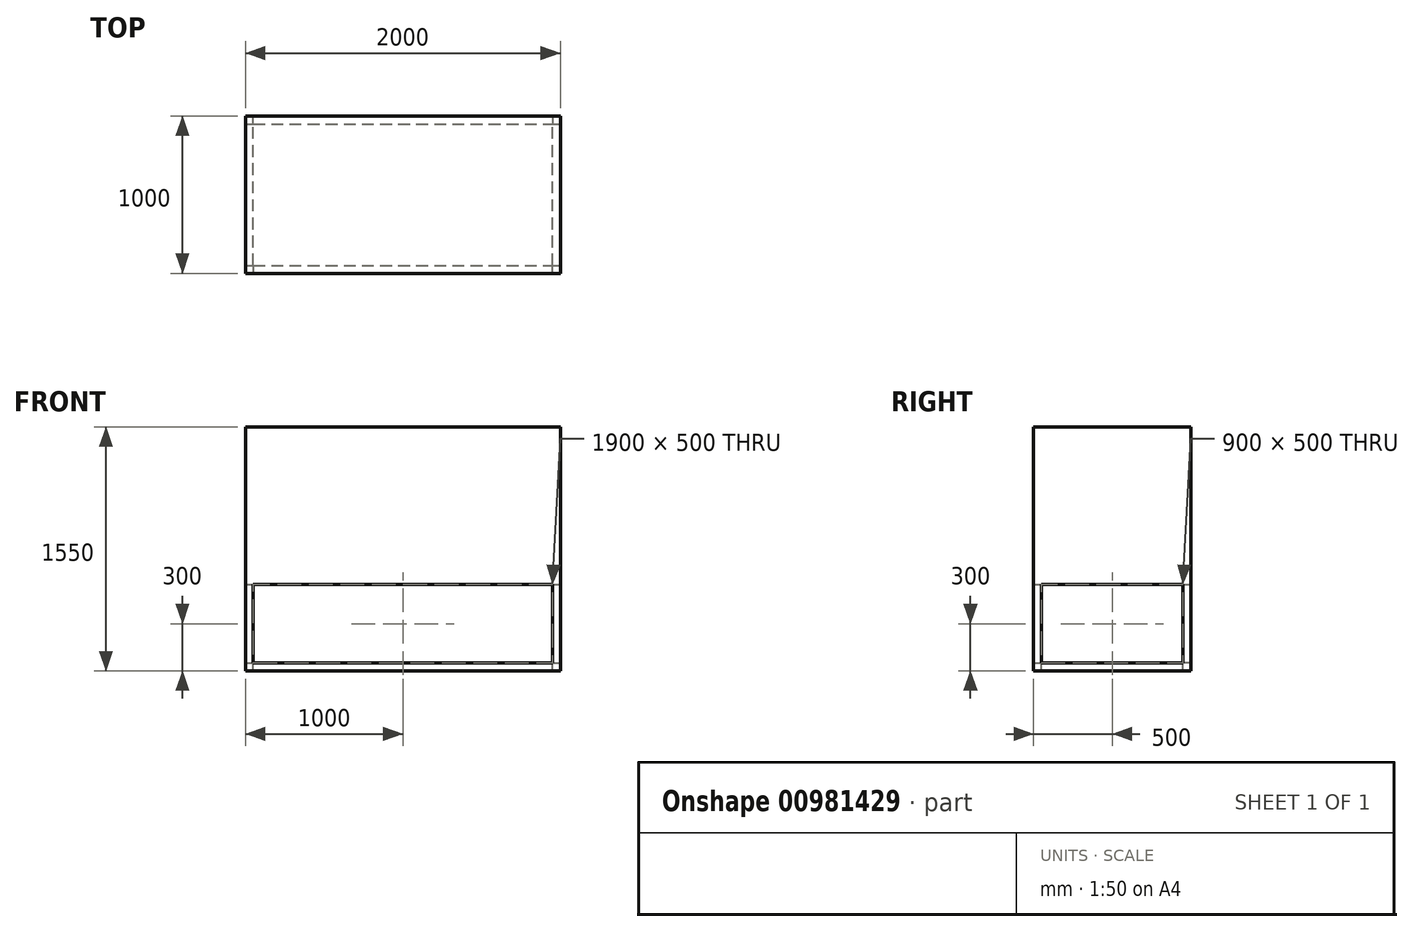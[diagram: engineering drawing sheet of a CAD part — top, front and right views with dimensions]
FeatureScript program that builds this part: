
annotation { "Feature Type Name" : "Feature", "Feature Type Description" : "" }
export const myFeature = defineFeature(function(context is Context, id is Id, definition is map)
    precondition{}
    {
        {
            var Q0;
            Q0=qCreatedBy(makeId("Front.planeOp"),FACE);
            var sketch = newSketch(context, id + "F0", { "sketchPlane" : qUnion([Q0])});
            skLineSegment(sketch, "E0.bottom", {"start": v(-1000, 500) * mm, "end": v(1000, 500) * mm});
            skLineSegment(sketch, "E0.top", {"start": v(-1000, -500) * mm, "end": v(1000, -500) * mm});
            skLineSegment(sketch, "E0.left", {"start": v(-1000, 500) * mm, "end": v(-1000, -500) * mm});
            skLineSegment(sketch, "E0.right", {"start": v(1000, 500) * mm, "end": v(1000, -500) * mm});
            skPoint(sketch, "E0.middle", {"position": v(0, 0) * mm});
            skSolve(sketch);
        }
        {
            var Q0;
            Q0 = qSketchRegion(id + "F0", true);
            extrude(context, id + "F1", {"entities" : qUnion([Q0]), "depth" : 1000 * mm, "offsetDistance" : 25 * mm});
        }
        {
            var Q0;
            Q0=makeQuery(id+"F1.opExtrude","SWEPT_FACE",FACE,{"disambiguationData":[OSD([sQuery(id+"F0.wireOp",EDGE,"E0.top")])]});
            cPlane(context, id + "F2", {"entities" : qUnion([Q0]), "cplaneType" : CPlaneType.OFFSET, "offset" : 0 * mm, "width" : 150 * mm, "height" : 150 * mm});
        }
        {
            var Q0;
            Q0=qCreatedBy(id+"F2.planeOp",FACE);
            var sketch = newSketch(context, id + "F3", { "sketchPlane" : qUnion([Q0])});
            skLineSegment(sketch, "E1", {"start": v(1000, 0) * mm, "end": v(1000, 50) * mm});
            skLineSegment(sketch, "E2", {"start": v(1000, 1000) * mm, "end": v(950, 1000) * mm});
            skLineSegment(sketch, "E3", {"start": v(-1000, 1000) * mm, "end": v(-1000, 950) * mm});
            skLineSegment(sketch, "E4", {"start": v(-1000, 0) * mm, "end": v(-950, 0) * mm});
            skLineSegment(sketch, "E5", {"start": v(-1000, 50) * mm, "end": v(-950, 50) * mm});
            skLineSegment(sketch, "E6", {"start": v(-1000, 950) * mm, "end": v(-950, 950) * mm});
            skLineSegment(sketch, "E7", {"start": v(-950, 950) * mm, "end": v(-950, 1000) * mm});
            skLineSegment(sketch, "E8", {"start": v(950, 1000) * mm, "end": v(950, 950) * mm});
            skLineSegment(sketch, "E9", {"start": v(950, 950) * mm, "end": v(1000, 950) * mm});
            skLineSegment(sketch, "E10", {"start": v(950, 0) * mm, "end": v(950, 50) * mm});
            skLineSegment(sketch, "E11", {"start": v(950, 50) * mm, "end": v(1000, 50) * mm});
            skLineSegment(sketch, "E12", {"start": v(-950, 50) * mm, "end": v(-950, 0) * mm});
            skLineSegment(sketch, "E13.trimOffspring", {"start": v(-950, 1000) * mm, "end": v(-1000, 1000) * mm});
            skLineSegment(sketch, "E14.trimOffspring", {"start": v(1000, 950) * mm, "end": v(1000, 1000) * mm});
            skLineSegment(sketch, "E15.trimOffspring", {"start": v(950, 0) * mm, "end": v(1000, 0) * mm});
            skLineSegment(sketch, "E16.trimOffspring", {"start": v(-1000, 50) * mm, "end": v(-1000, 0) * mm});
            skSolve(sketch);
        }
        {
            var Q0;
            Q0 = qSketchRegion(id + "F3", true);
            extrude(context, id + "F4", {"entities" : qUnion([Q0]), "operationType" : NewBodyOperationType.ADD, "depth" : 500 * mm, "offsetDistance" : 25 * mm});
        }
        {
            var Q0;
            Q0=makeQuery(id+"F4.opExtrude","CAP_FACE",FACE,{"disambiguationData":[OSD([sQuery(id+"F3.wireOp",EDGE,"E3"),sQuery(id+"F3.wireOp",EDGE,"E6"),sQuery(id+"F3.wireOp",EDGE,"E7"),sQuery(id+"F3.wireOp",EDGE,"E13.trimOffspring")])],"isStart":false});
            cPlane(context, id + "F5", {"entities" : qUnion([Q0]), "cplaneType" : CPlaneType.OFFSET, "offset" : 0 * mm, "width" : 150 * mm, "height" : 150 * mm});
        }
        {
            var Q0;
            Q0=qCreatedBy(id+"F5.planeOp",FACE);
            var sketch = newSketch(context, id + "F6", { "sketchPlane" : qUnion([Q0])});
            skLineSegment(sketch, "E17.bottom", {"start": v(-1000, 1000) * mm, "end": v(1000, 1000) * mm});
            skLineSegment(sketch, "E17.top", {"start": v(-1000, 0) * mm, "end": v(1000, 0) * mm});
            skLineSegment(sketch, "E17.left", {"start": v(-1000, 1000) * mm, "end": v(-1000, 0) * mm});
            skLineSegment(sketch, "E17.right", {"start": v(1000, 1000) * mm, "end": v(1000, 0) * mm});
            skLineSegment(sketch, "E18.0", {"start": v(-950, 950) * mm, "end": v(950, 950) * mm});
            skLineSegment(sketch, "E18.1", {"start": v(-950, 950) * mm, "end": v(-950, 50) * mm});
            skLineSegment(sketch, "E18.2", {"start": v(-950, 50) * mm, "end": v(950, 50) * mm});
            skLineSegment(sketch, "E18.3", {"start": v(950, 950) * mm, "end": v(950, 50) * mm});
            skSolve(sketch);
        }
        {
            var Q0;
            Q0 = qSketchRegion(id + "F6", true);
            extrude(context, id + "F7", {"entities" : qUnion([Q0]), "operationType" : NewBodyOperationType.ADD, "depth" : 50 * mm, "offsetDistance" : 25 * mm});
        }
    });
